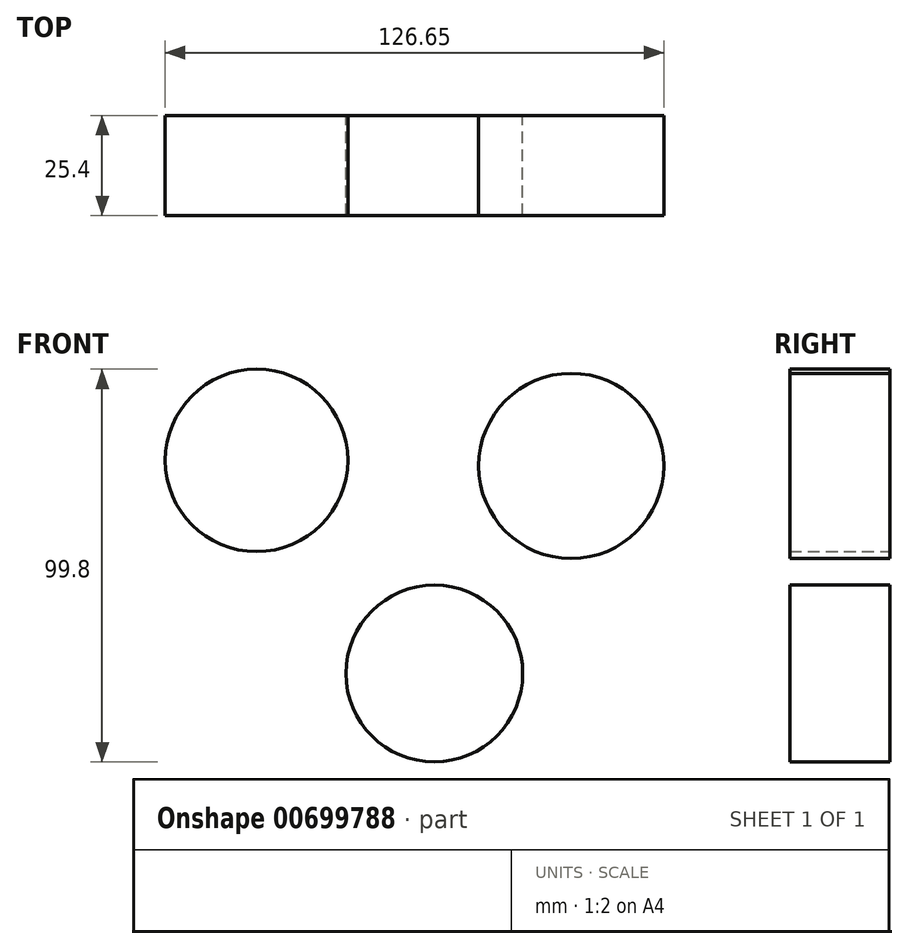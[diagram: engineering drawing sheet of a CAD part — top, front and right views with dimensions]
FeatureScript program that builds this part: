
annotation { "Feature Type Name" : "Feature", "Feature Type Description" : "" }
export const myFeature = defineFeature(function(context is Context, id is Id, definition is map)
    precondition{}
    {
        {
            var Q0;
            Q0=qCreatedBy(makeId("Front.planeOp"),FACE);
            var sketch = newSketch(context, id + "F0", { "sketchPlane" : qUnion([Q0])});
            skCircle(sketch, "E0", {"center": v(0, 0) * mm, "radius": 22.45 * mm});
            skCircle(sketch, "E1", {"center": v(-45.18, 54.16) * mm, "radius": 23.18 * mm});
            skCircle(sketch, "E2", {"center": v(34.77, 52.74) * mm, "radius": 23.52 * mm});
            skSolve(sketch);
        }
        {
            var Q0;
            Q0 = qSketchRegion(id + "F0", true);
            extrude(context, id + "F1", {"entities" : qUnion([Q0]), "depth" : 25.4 * mm, "offsetDistance" : 25.4 * mm});
        }
    });
